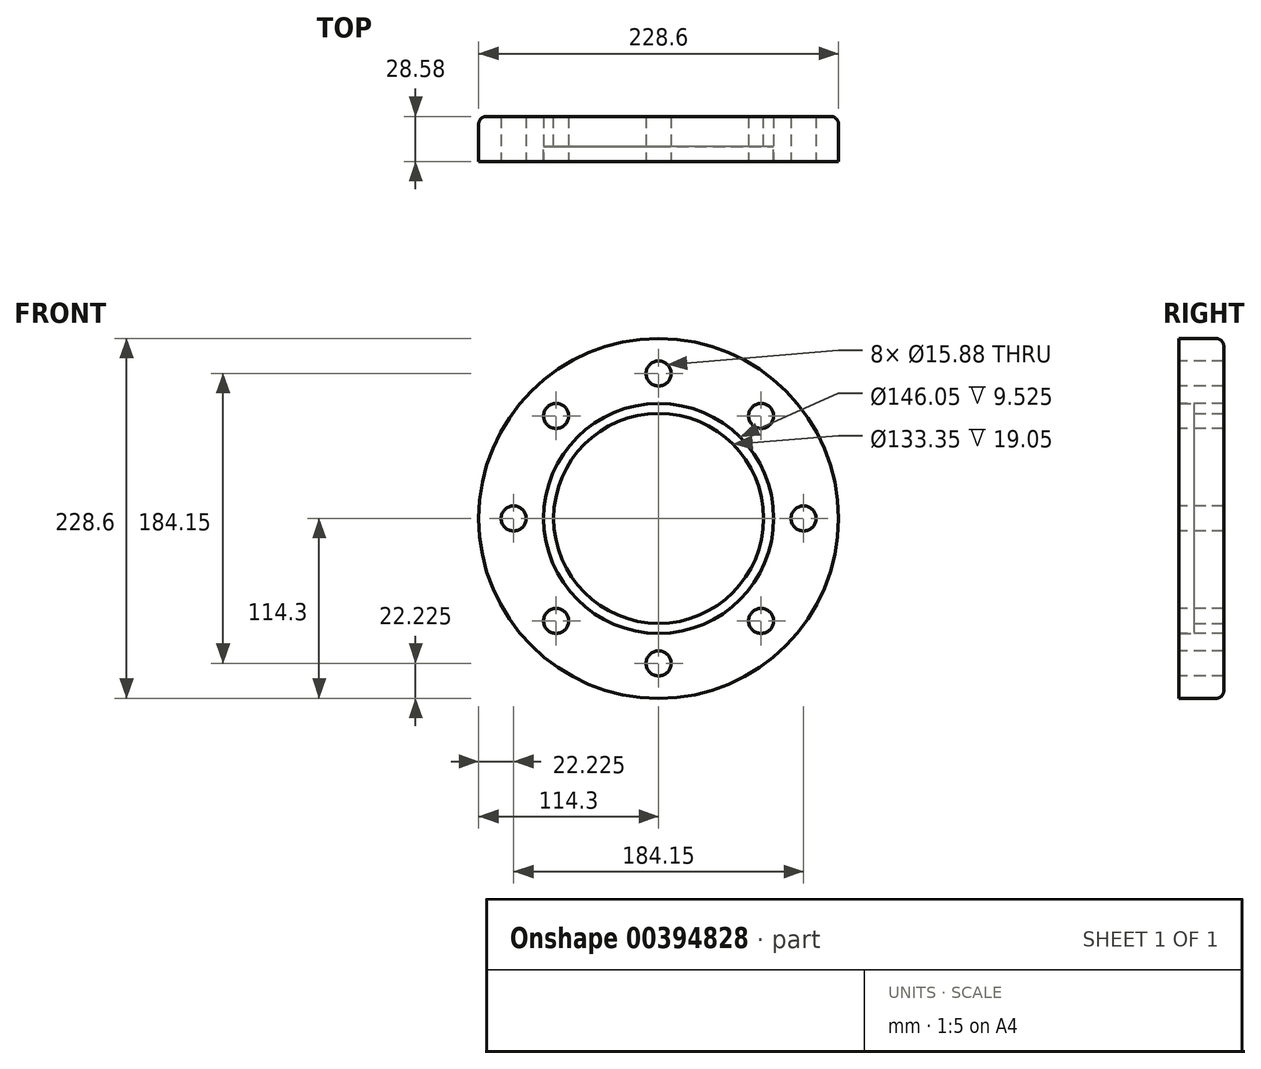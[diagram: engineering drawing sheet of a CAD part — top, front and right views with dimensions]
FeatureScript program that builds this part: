
annotation { "Feature Type Name" : "Feature", "Feature Type Description" : "" }
export const myFeature = defineFeature(function(context is Context, id is Id, definition is map)
    precondition{}
    {
        {
            var Q0;
            Q0=qCreatedBy(makeId("Right.planeOp"),FACE);
            var sketch = newSketch(context, id + "F0", { "sketchPlane" : qUnion([Q0])});
            skLineSegment(sketch, "E0", {"start": v(52.3, 0) * mm, "end": v(-51.3, 0) * mm, "construction": true});
            skLineSegment(sketch, "E1", {"start": v(0, 58.82) * mm, "end": v(0, -54.81) * mm, "construction": true});
            skLineSegment(sketch, "E2", {"start": v(0, 114.3) * mm, "end": v(0, 73.03) * mm});
            skLineSegment(sketch, "E3", {"start": v(0, 73.03) * mm, "end": v(9.53, 73.03) * mm});
            skLineSegment(sketch, "E4", {"start": v(9.53, 73.03) * mm, "end": v(9.53, 66.68) * mm});
            skLineSegment(sketch, "E5", {"start": v(9.53, 66.68) * mm, "end": v(28.58, 66.68) * mm});
            skLineSegment(sketch, "E6", {"start": v(28.58, 66.68) * mm, "end": v(28.58, 114.3) * mm});
            skLineSegment(sketch, "E7", {"start": v(28.58, 114.3) * mm, "end": v(0, 114.3) * mm});
            skSolve(sketch);
        }
        {
            var Q0;
            Q0=qSketchRegion(id+"F0",true);
            var Q1;
            Q1=sQuery(id+"F0.wireOp",EDGE,"E0");
            revolve(context, id + "F1", {"entities" : qUnion([Q0]), "axis" : qUnion([Q1]), "revolveType" : RevolveType.FULL});
        }
        {
            var Q0;
            Q0=makeQuery(id+"F1.opRevolve","SWEPT_FACE",FACE,{"disambiguationData":[OSD([sQuery(id+"F0.wireOp",EDGE,"E2")])]});
            var sketch = newSketch(context, id + "F2", { "sketchPlane" : qUnion([Q0])});
            skCircle(sketch, "E8", {"center": v(0, 92.08) * mm, "radius": 7.94 * mm});
            skCircle(sketch, "E9.1.0", {"center": v(-65.1, 65.1) * mm, "radius": 7.94 * mm});
            skCircle(sketch, "E9.2.0", {"center": v(-92.08, 0) * mm, "radius": 7.94 * mm});
            skCircle(sketch, "E9.3.0", {"center": v(-65.1, -65.1) * mm, "radius": 7.94 * mm});
            skCircle(sketch, "E9.4.0", {"center": v(0, -92.08) * mm, "radius": 7.94 * mm});
            skCircle(sketch, "E9.5.0", {"center": v(65.1, -65.1) * mm, "radius": 7.94 * mm});
            skCircle(sketch, "E9.6.0", {"center": v(92.08, 0) * mm, "radius": 7.94 * mm});
            skCircle(sketch, "E9.7.0", {"center": v(65.1, 65.1) * mm, "radius": 7.94 * mm});
            skPoint(sketch, "E9.center", {"position": v(0, 0) * mm});
            skSolve(sketch);
        }
        {
            var Q0;
            Q0=qSketchRegion(id+"F2",true);
            extrude(context, id + "F3", {"entities" : qUnion([Q0]), "operationType" : NewBodyOperationType.REMOVE, "endBound" : BoundingType.THROUGH_ALL, "oppositeDirection" : true, "depth" : 25.4 * mm});
        }
        {
            var Q0;
            Q0=makeQuery(id+"F1.opRevolve","SWEPT_EDGE",EDGE,{"disambiguationData":[OSD([sQuery(id+"F0.wireOp",EDGE,"E6"),sQuery(id+"F0.wireOp",EDGE,"E7")])]});
            fillet(context, id + "F4", {"entities" : qUnion([Q0]), "radius" : 5.08 * mm, "tangentPropagation" : true, "allowEdgeOverflow" : false});
        }
    });
